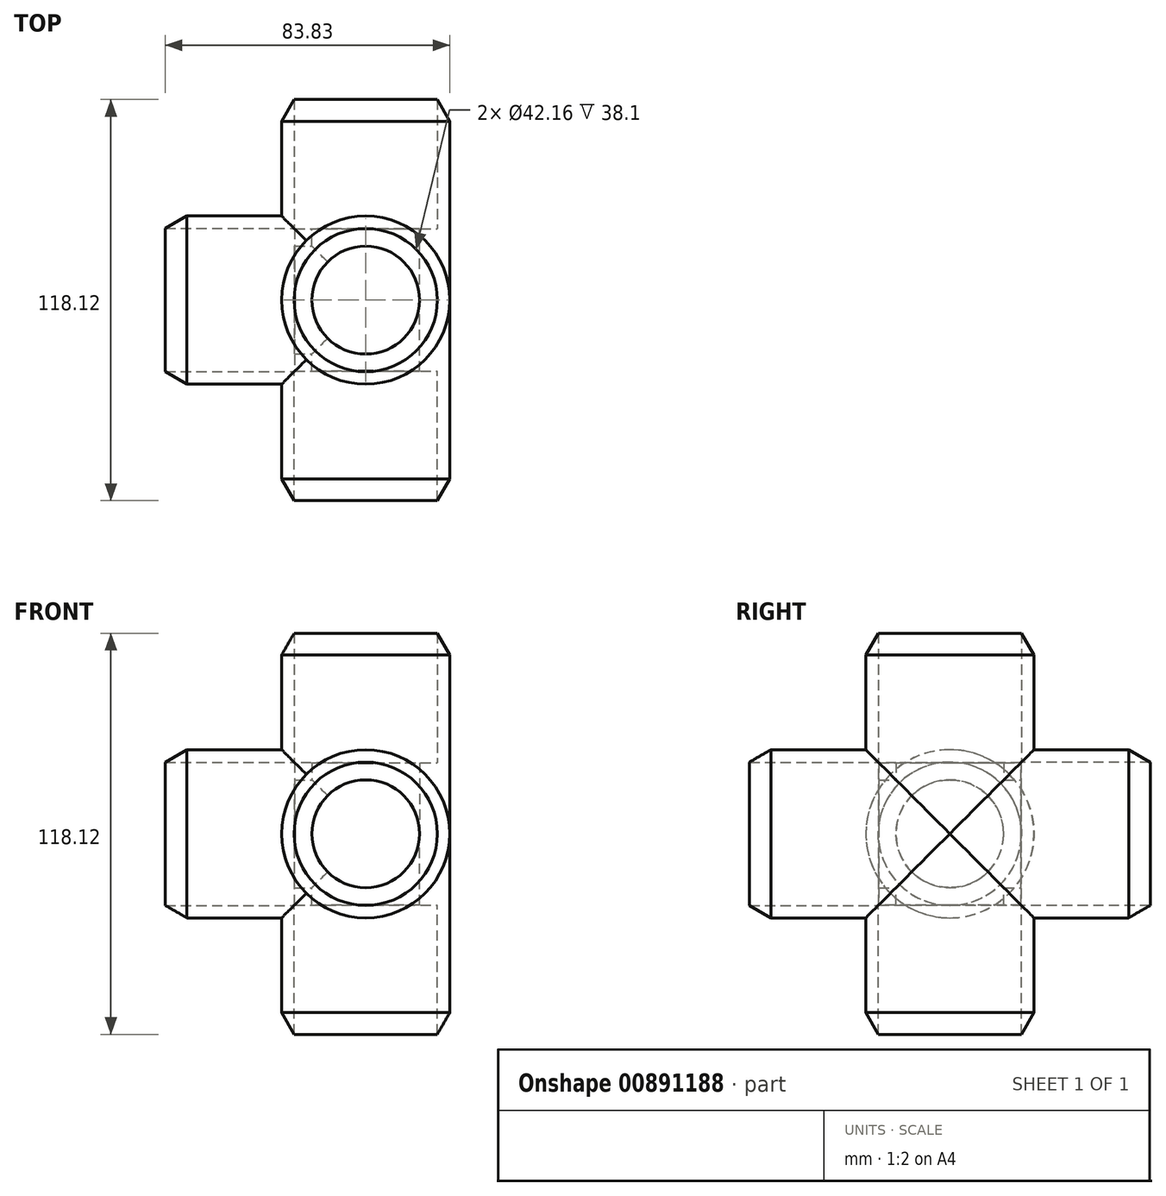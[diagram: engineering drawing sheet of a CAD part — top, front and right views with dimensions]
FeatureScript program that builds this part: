
annotation { "Feature Type Name" : "Feature", "Feature Type Description" : "" }
export const myFeature = defineFeature(function(context is Context, id is Id, definition is map)
    precondition{}
    {
        {
            var Q0;
            Q0=qCreatedBy(makeId("Right.planeOp"),FACE);
            var sketch = newSketch(context, id + "F0", { "sketchPlane" : qUnion([Q0])});
            skLineSegment(sketch, "E0", {"start": v(-59.06, 21.08) * mm, "end": v(-20.96, 21.08) * mm});
            skLineSegment(sketch, "E1", {"start": v(-20.96, 21.08) * mm, "end": v(-20.96, 15.88) * mm});
            skLineSegment(sketch, "E2", {"start": v(-20.96, 15.88) * mm, "end": v(0, 15.88) * mm});
            skLineSegment(sketch, "E3", {"start": v(15.87, 0) * mm, "end": v(15.87, 0) * mm});
            skLineSegment(sketch, "E4", {"start": v(15.87, 0) * mm, "end": v(24.77, 0) * mm});
            skLineSegment(sketch, "E5", {"start": v(24.77, 0) * mm, "end": v(24.77, 0) * mm});
            skLineSegment(sketch, "E6", {"start": v(0, 24.77) * mm, "end": v(-52.68, 24.76) * mm});
            skLineSegment(sketch, "E7", {"start": v(-52.68, 24.76) * mm, "end": v(-59.06, 21.08) * mm});
            skArc(sketch, "E8.filletArc", {"start": v(24.77, 0) * mm, "mid": v(17.51, 17.51) * mm, "end": v(0, 24.77) * mm});
            skArc(sketch, "E9.filletArc", {"start": v(15.88, 0) * mm, "mid": v(11.23, 11.23) * mm, "end": v(0, 15.88) * mm});
            skLineSegment(sketch, "E10", {"start": v(0, 0) * mm, "end": v(0, -11.7) * mm});
            skLineSegment(sketch, "E11", {"start": v(0, 0) * mm, "end": v(10.52, 0) * mm});
            skLineSegment(sketch, "E12", {"start": v(-59.06, 21.08) * mm, "end": v(-59.06, 0) * mm});
            skLineSegment(sketch, "E13", {"start": v(-59.06, 0) * mm, "end": v(15.87, 0) * mm});
            skSolve(sketch);
        }
        {
            var Q0;
            Q0=qCreatedBy(makeId("Right.planeOp"),FACE);
            var sketch = newSketch(context, id + "F1", { "sketchPlane" : qUnion([Q0])});
            skLineSegment(sketch, "E14", {"start": v(-21.08, -59.06) * mm, "end": v(-21.08, -20.96) * mm});
            skLineSegment(sketch, "E15", {"start": v(-21.08, -20.96) * mm, "end": v(-15.88, -20.96) * mm});
            skLineSegment(sketch, "E16", {"start": v(-15.88, -20.96) * mm, "end": v(-15.88, 0) * mm});
            skLineSegment(sketch, "E17", {"start": v(0, 15.88) * mm, "end": v(0, 15.88) * mm});
            skLineSegment(sketch, "E18", {"start": v(0, 15.88) * mm, "end": v(0, 24.77) * mm});
            skLineSegment(sketch, "E19", {"start": v(0, 24.77) * mm, "end": v(0, 24.77) * mm});
            skLineSegment(sketch, "E20", {"start": v(-24.77, 0) * mm, "end": v(-24.76, -52.68) * mm});
            skLineSegment(sketch, "E21", {"start": v(-24.76, -52.68) * mm, "end": v(-21.08, -59.06) * mm});
            skArc(sketch, "E22.filletArc", {"start": v(0, 24.77) * mm, "mid": v(-17.51, 17.51) * mm, "end": v(-24.77, 0) * mm});
            skArc(sketch, "E23.filletArc", {"start": v(0, 15.88) * mm, "mid": v(-11.23, 11.23) * mm, "end": v(-15.88, 0) * mm});
            skLineSegment(sketch, "E24", {"start": v(0, 36.04) * mm, "end": v(0, 0) * mm});
            skLineSegment(sketch, "E25", {"start": v(-2.18, 0) * mm, "end": v(0, 0) * mm});
            skLineSegment(sketch, "E26", {"start": v(-21.08, -59.06) * mm, "end": v(0, -59.06) * mm});
            skLineSegment(sketch, "E27", {"start": v(0, -59.06) * mm, "end": v(0, 15.88) * mm});
            skSolve(sketch);
        }
        {
            var Q0;
            Q0=qCreatedBy(makeId("Right.planeOp"),FACE);
            var sketch = newSketch(context, id + "F2", { "sketchPlane" : qUnion([Q0])});
            skLineSegment(sketch, "E28", {"start": v(59.06, -21.08) * mm, "end": v(20.96, -21.08) * mm});
            skLineSegment(sketch, "E29", {"start": v(20.96, -21.08) * mm, "end": v(20.96, -15.88) * mm});
            skLineSegment(sketch, "E30", {"start": v(20.96, -15.88) * mm, "end": v(0, -15.88) * mm});
            skLineSegment(sketch, "E31", {"start": v(-15.87, 0) * mm, "end": v(-15.87, 0) * mm});
            skLineSegment(sketch, "E32", {"start": v(-15.87, 0) * mm, "end": v(-24.77, 0) * mm});
            skLineSegment(sketch, "E33", {"start": v(-24.77, 0) * mm, "end": v(-24.77, 0) * mm});
            skLineSegment(sketch, "E34", {"start": v(0, -24.77) * mm, "end": v(52.68, -24.76) * mm});
            skLineSegment(sketch, "E35", {"start": v(52.68, -24.77) * mm, "end": v(59.06, -21.08) * mm});
            skArc(sketch, "E36.filletArc", {"start": v(-24.77, 0) * mm, "mid": v(-17.51, -17.51) * mm, "end": v(0, -24.77) * mm});
            skArc(sketch, "E37.filletArc", {"start": v(-15.88, 0) * mm, "mid": v(-11.23, -11.23) * mm, "end": v(0, -15.88) * mm});
            skLineSegment(sketch, "E38", {"start": v(0, 2.6) * mm, "end": v(0, 0) * mm});
            skLineSegment(sketch, "E39", {"start": v(0, 0) * mm, "end": v(10.52, 0) * mm});
            skLineSegment(sketch, "E40", {"start": v(59.06, -21.08) * mm, "end": v(59.06, 0) * mm});
            skLineSegment(sketch, "E41", {"start": v(59.06, 0) * mm, "end": v(-15.87, 0) * mm});
            skSolve(sketch);
        }
        {
            var Q0;
            Q0=qCreatedBy(makeId("Right.planeOp"),FACE);
            var sketch = newSketch(context, id + "F3", { "sketchPlane" : qUnion([Q0])});
            skLineSegment(sketch, "E42", {"start": v(21.08, 59.06) * mm, "end": v(21.08, 20.95) * mm});
            skLineSegment(sketch, "E43", {"start": v(21.08, 20.95) * mm, "end": v(15.88, 20.95) * mm});
            skLineSegment(sketch, "E44", {"start": v(15.88, 20.96) * mm, "end": v(15.88, 0) * mm});
            skLineSegment(sketch, "E45", {"start": v(0, -15.88) * mm, "end": v(0, -15.88) * mm});
            skLineSegment(sketch, "E46", {"start": v(0, -15.88) * mm, "end": v(0, -24.77) * mm});
            skLineSegment(sketch, "E47", {"start": v(0, -24.77) * mm, "end": v(0, -24.77) * mm});
            skLineSegment(sketch, "E48", {"start": v(24.77, 0) * mm, "end": v(24.76, 52.68) * mm});
            skLineSegment(sketch, "E49", {"start": v(24.76, 52.68) * mm, "end": v(21.08, 59.06) * mm});
            skArc(sketch, "E50.filletArc", {"start": v(0, -24.77) * mm, "mid": v(17.51, -17.51) * mm, "end": v(24.77, 0) * mm});
            skArc(sketch, "E51.filletArc", {"start": v(0, -15.88) * mm, "mid": v(11.23, -11.23) * mm, "end": v(15.88, 0) * mm});
            skLineSegment(sketch, "E52", {"start": v(0, 9.3) * mm, "end": v(0, 0) * mm});
            skLineSegment(sketch, "E53", {"start": v(-7.4, 0) * mm, "end": v(0, 0) * mm});
            skLineSegment(sketch, "E54", {"start": v(21.08, 59.05) * mm, "end": v(0, 59.05) * mm});
            skLineSegment(sketch, "E55", {"start": v(0, 59.05) * mm, "end": v(0, -15.88) * mm});
            skSolve(sketch);
        }
        {
            var Q0;
            Q0=qCreatedBy(makeId("Top.planeOp"),FACE);
            var sketch = newSketch(context, id + "F4", { "sketchPlane" : qUnion([Q0])});
            skLineSegment(sketch, "E56", {"start": v(-59.06, 21.08) * mm, "end": v(-20.96, 21.08) * mm});
            skLineSegment(sketch, "E57", {"start": v(-20.96, 21.08) * mm, "end": v(-20.96, 15.88) * mm});
            skLineSegment(sketch, "E58", {"start": v(-20.96, 15.88) * mm, "end": v(0, 15.88) * mm});
            skLineSegment(sketch, "E59", {"start": v(15.88, 0) * mm, "end": v(15.88, 0) * mm});
            skLineSegment(sketch, "E60", {"start": v(15.88, 0) * mm, "end": v(24.77, 0) * mm});
            skLineSegment(sketch, "E61", {"start": v(24.77, 0) * mm, "end": v(24.77, 0) * mm});
            skLineSegment(sketch, "E62", {"start": v(0, 24.77) * mm, "end": v(-52.68, 24.76) * mm});
            skLineSegment(sketch, "E63", {"start": v(-52.68, 24.76) * mm, "end": v(-59.06, 21.08) * mm});
            skArc(sketch, "E64.filletArc", {"start": v(24.77, 0) * mm, "mid": v(17.51, 17.51) * mm, "end": v(0, 24.77) * mm});
            skArc(sketch, "E65.filletArc", {"start": v(15.88, 0) * mm, "mid": v(11.23, 11.23) * mm, "end": v(0, 15.88) * mm});
            skLineSegment(sketch, "E66", {"start": v(0, 15.42) * mm, "end": v(0, 0) * mm});
            skLineSegment(sketch, "E67", {"start": v(-12.56, 0) * mm, "end": v(0, 0) * mm});
            skLineSegment(sketch, "E68", {"start": v(-59.06, 21.08) * mm, "end": v(-59.06, 0) * mm});
            skLineSegment(sketch, "E69", {"start": v(-59.06, 0) * mm, "end": v(15.87, 0) * mm});
            skSolve(sketch);
        }
        {
            var Q0;
            Q0=qSketchRegion(id+"F0",true);
            var Q1;
            Q1=sQuery(id+"F0.wireOp",EDGE,"E13");
            revolve(context, id + "F5", {"surfaceOperationType" : NewSurfaceOperationType.NEW, "entities" : qUnion([Q0]), "axis" : qUnion([Q1]), "revolveType" : RevolveType.FULL});
        }
        {
            var Q0;
            {var subQ4=makeQuery(id+"F1.imprint","IMPRINT",EDGE,{"derivedFrom":sQuery(id+"F1.wireOp",EDGE,"E14")});Q0=qUnion([makeQuery(id+"F1.imprint","IMPRINT",FACE,{"disambiguationData":[TD([[subQ4,1.0]])]}),makeQuery(id+"F1.imprint","IMPRINT",FACE,{"disambiguationData":[TD([[subQ4,-1.0]])]})]);}
            var Q1;
            Q1=sQuery(id+"F1.wireOp",EDGE,"E27");
            revolve(context, id + "F6", {"operationType" : NewBodyOperationType.ADD, "surfaceOperationType" : NewSurfaceOperationType.NEW, "entities" : qUnion([Q0]), "axis" : qUnion([Q1]), "revolveType" : RevolveType.FULL});
        }
        {
            var Q0;
            Q0=qSketchRegion(id+"F2",true);
            var Q1;
            Q1=sQuery(id+"F2.wireOp",EDGE,"E41");
            revolve(context, id + "F7", {"operationType" : NewBodyOperationType.ADD, "surfaceOperationType" : NewSurfaceOperationType.NEW, "entities" : qUnion([Q0]), "axis" : qUnion([Q1]), "revolveType" : RevolveType.FULL});
        }
        {
            var Q0;
            Q0=qSketchRegion(id+"F3",true);
            var Q1;
            Q1=sQuery(id+"F3.wireOp",EDGE,"E55");
            revolve(context, id + "F8", {"operationType" : NewBodyOperationType.ADD, "surfaceOperationType" : NewSurfaceOperationType.NEW, "entities" : qUnion([Q0]), "axis" : qUnion([Q1]), "revolveType" : RevolveType.FULL});
        }
        {
            var Q0;
            Q0=qSketchRegion(id+"F4",true);
            var Q1;
            Q1=sQuery(id+"F4.wireOp",EDGE,"E69");
            revolve(context, id + "F9", {"operationType" : NewBodyOperationType.ADD, "surfaceOperationType" : NewSurfaceOperationType.NEW, "entities" : qUnion([Q0]), "axis" : qUnion([Q1]), "revolveType" : RevolveType.FULL});
        }
        {
            var Q0;
            Q0=makeQuery(id+"F0.imprint","IMPRINT",FACE,{"disambiguationData":[TD([[makeQuery(id+"F0.imprint","IMPRINT",EDGE,{"derivedFrom":sQuery(id+"F0.wireOp",EDGE,"E0")}),-1.0]])]});
            var Q1;
            Q1=sQuery(id+"F0.wireOp",EDGE,"E13");
            revolve(context, id + "F10", {"operationType" : NewBodyOperationType.REMOVE, "surfaceOperationType" : NewSurfaceOperationType.NEW, "entities" : qUnion([Q0]), "axis" : qUnion([Q1]), "revolveType" : RevolveType.FULL, "oppositeDirection" : true});
        }
        {
            var Q0;
            Q0=makeQuery(id+"F1.imprint","IMPRINT",FACE,{"disambiguationData":[TD([[makeQuery(id+"F1.imprint","IMPRINT",EDGE,{"derivedFrom":sQuery(id+"F1.wireOp",EDGE,"E14")}),-1.0]])]});
            var Q1;
            Q1=sQuery(id+"F1.wireOp",EDGE,"E27");
            revolve(context, id + "F11", {"operationType" : NewBodyOperationType.REMOVE, "surfaceOperationType" : NewSurfaceOperationType.NEW, "entities" : qUnion([Q0]), "axis" : qUnion([Q1]), "revolveType" : RevolveType.FULL, "oppositeDirection" : true});
        }
        {
            var Q0;
            Q0=makeQuery(id+"F2.imprint","IMPRINT",FACE,{"disambiguationData":[TD([[makeQuery(id+"F2.imprint","IMPRINT",EDGE,{"derivedFrom":sQuery(id+"F2.wireOp",EDGE,"E28")}),-1.0]])]});
            var Q1;
            Q1=sQuery(id+"F2.wireOp",EDGE,"E41");
            revolve(context, id + "F12", {"operationType" : NewBodyOperationType.REMOVE, "surfaceOperationType" : NewSurfaceOperationType.NEW, "entities" : qUnion([Q0]), "axis" : qUnion([Q1]), "revolveType" : RevolveType.FULL, "oppositeDirection" : true});
        }
        {
            var Q0;
            Q0=makeQuery(id+"F3.imprint","IMPRINT",FACE,{"disambiguationData":[TD([[makeQuery(id+"F3.imprint","IMPRINT",EDGE,{"derivedFrom":sQuery(id+"F3.wireOp",EDGE,"E42")}),-1.0]])]});
            var Q1;
            Q1=sQuery(id+"F3.wireOp",EDGE,"E55");
            revolve(context, id + "F13", {"operationType" : NewBodyOperationType.REMOVE, "surfaceOperationType" : NewSurfaceOperationType.NEW, "entities" : qUnion([Q0]), "axis" : qUnion([Q1]), "revolveType" : RevolveType.FULL, "oppositeDirection" : true});
        }
        {
            var Q0;
            Q0=makeQuery(id+"F4.imprint","IMPRINT",FACE,{"disambiguationData":[TD([[makeQuery(id+"F4.imprint","IMPRINT",EDGE,{"derivedFrom":sQuery(id+"F4.wireOp",EDGE,"E56")}),-1.0]])]});
            var Q1;
            Q1=sQuery(id+"F4.wireOp",EDGE,"E69");
            revolve(context, id + "F14", {"operationType" : NewBodyOperationType.REMOVE, "surfaceOperationType" : NewSurfaceOperationType.NEW, "entities" : qUnion([Q0]), "axis" : qUnion([Q1]), "revolveType" : RevolveType.FULL, "oppositeDirection" : true});
        }
    });
